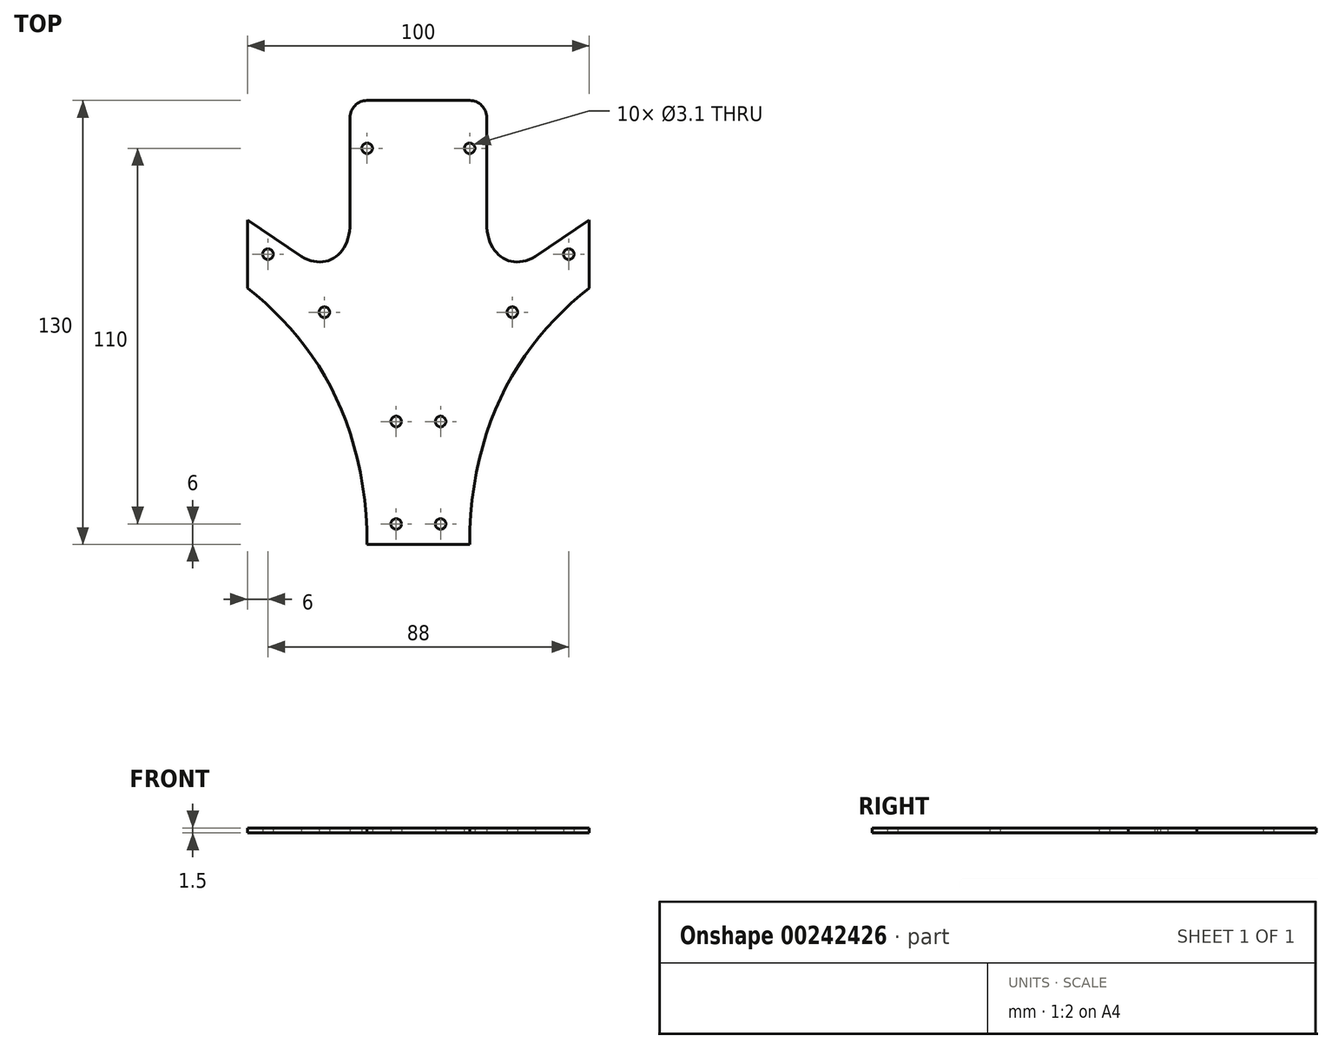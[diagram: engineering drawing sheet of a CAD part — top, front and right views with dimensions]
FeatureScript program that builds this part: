
annotation { "Feature Type Name" : "Feature", "Feature Type Description" : "" }
export const myFeature = defineFeature(function(context is Context, id is Id, definition is map)
    precondition{}
    {
        {
            var Q0;
            Q0=qCreatedBy(makeId("Top.planeOp"),FACE);
            var sketch = newSketch(context, id + "F0", { "sketchPlane" : qUnion([Q0])});
            skLineSegment(sketch, "E0", {"start": v(50.03, 65) * mm, "end": v(-50.03, -65) * mm, "construction": true});
            skSolve(sketch);
        }
        {
            var Q0;
            Q0=qCreatedBy(makeId("Top.planeOp"),FACE);
            var sketch = newSketch(context, id + "F1", { "sketchPlane" : qUnion([Q0])});
            skLineSegment(sketch, "E1", {"start": v(0, 65) * mm, "end": v(-15, 65) * mm});
            skLineSegment(sketch, "E2", {"start": v(-20, 60) * mm, "end": v(-20, 29) * mm});
            skLineSegment(sketch, "E3", {"start": v(-34.25, 19.38) * mm, "end": v(-50, 30) * mm});
            skLineSegment(sketch, "E4", {"start": v(-50, 30) * mm, "end": v(-50, 10) * mm});
            skLineSegment(sketch, "E5", {"start": v(-15, -65) * mm, "end": v(0, -65) * mm});
            skFitSpline(sketch, "E6", {"points": [v(-20, 29) * mm, v(-34.25, 19.38) * mm], "startDerivative": vector(0, -28.2) * mm, "endDerivative": vector(-21.27, 13.01) * mm});
            skFitSpline(sketch, "E7", {"points": [v(-50, 10) * mm, v(-15, -65) * mm], "startDerivative": vector(61.4, -47.18) * mm, "endDerivative": vector(0, -103.13) * mm});
            skLineSegment(sketch, "E8", {"start": v(0, 65) * mm, "end": v(0, -65) * mm, "construction": true});
            skCircle(sketch, "E9", {"center": v(-6.5, -59) * mm, "radius": 1.55 * mm});
            skCircle(sketch, "E10", {"center": v(-27.5, 3) * mm, "radius": 1.55 * mm});
            skCircle(sketch, "E11", {"center": v(-44, 20) * mm, "radius": 1.55 * mm});
            skCircle(sketch, "E12", {"center": v(-15, 51) * mm, "radius": 1.55 * mm});
            skCircle(sketch, "E13", {"center": v(-6.5, -29) * mm, "radius": 1.55 * mm});
            skPoint(sketch, "E14.visualSharp", {"position": v(-20, 65) * mm});
            skArc(sketch, "E14.filletArc", {"start": v(-15, 65) * mm, "mid": v(-18.54, 63.54) * mm, "end": v(-20, 60) * mm});
            skLineSegment(sketch, "E15.MirrorCS", {"start": v(0, 65) * mm, "end": v(15, 65) * mm});
            skArc(sketch, "E16.MirrorCS", {"start": v(15, 65) * mm, "mid": v(18.54, 63.54) * mm, "end": v(20, 60) * mm});
            skCircle(sketch, "E17.MirrorC", {"center": v(15, 51) * mm, "radius": 1.55 * mm});
            skLineSegment(sketch, "E18.MirrorCS", {"start": v(20, 60) * mm, "end": v(20, 29) * mm});
            skFitSpline(sketch, "E19.MirrorCS", {"points": [v(20, 29) * mm, v(34.25, 19.38) * mm], "startDerivative": vector(0, -28.2) * mm, "endDerivative": vector(21.27, 13.01) * mm});
            skLineSegment(sketch, "E20.MirrorCS", {"start": v(34.25, 19.38) * mm, "end": v(50, 30) * mm});
            skLineSegment(sketch, "E21.MirrorCS", {"start": v(50, 30) * mm, "end": v(50, 10) * mm});
            skFitSpline(sketch, "E22.MirrorCS", {"points": [v(50, 10) * mm, v(15, -65) * mm], "startDerivative": vector(-61.4, -47.18) * mm, "endDerivative": vector(0, -103.13) * mm});
            skCircle(sketch, "E23.MirrorC", {"center": v(44, 20) * mm, "radius": 1.55 * mm});
            skCircle(sketch, "E24.MirrorC", {"center": v(27.5, 3) * mm, "radius": 1.55 * mm});
            skCircle(sketch, "E25.MirrorC", {"center": v(6.5, -29) * mm, "radius": 1.55 * mm});
            skCircle(sketch, "E26.MirrorC", {"center": v(6.5, -59) * mm, "radius": 1.55 * mm});
            skLineSegment(sketch, "E27.MirrorCS", {"start": v(15, -65) * mm, "end": v(0, -65) * mm});
            skSolve(sketch);
        }
        {
            var Q0;
            Q0=makeQuery(id+"F1.imprint","IMPRINT",FACE,{"disambiguationData":[TD([[makeQuery(id+"F1.imprint","IMPRINT",EDGE,{"derivedFrom":sQuery(id+"F1.wireOp",EDGE,"E1")}),1.0]])]});
            extrude(context, id + "F2", {"entities" : qUnion([Q0]), "depth" : 1.5 * mm, "offsetDistance" : 25 * mm});
        }
    });
